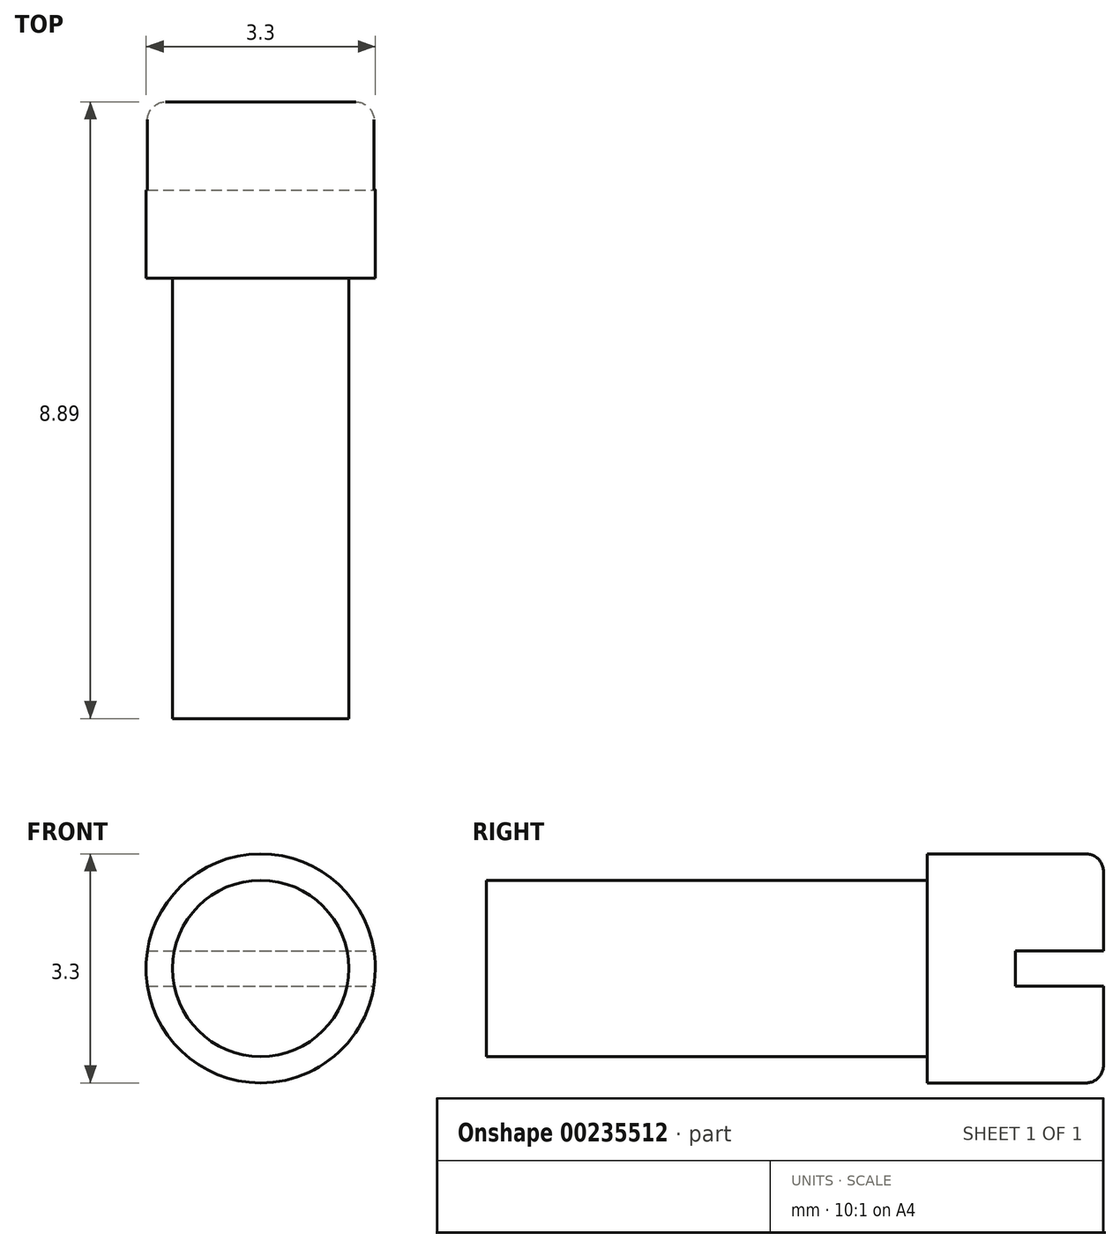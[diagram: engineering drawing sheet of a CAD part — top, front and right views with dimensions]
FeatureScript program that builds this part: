
annotation { "Feature Type Name" : "Feature", "Feature Type Description" : "" }
export const myFeature = defineFeature(function(context is Context, id is Id, definition is map)
    precondition{}
    {
        {
            var Q0;
            Q0=qCreatedBy(makeId("Front.planeOp"),FACE);
            var sketch = newSketch(context, id + "F0", { "sketchPlane" : qUnion([Q0])});
            skCircle(sketch, "E0", {"center": v(0, 0) * mm, "radius": 1.65 * mm});
            skCircle(sketch, "E1", {"center": v(0, 0) * mm, "radius": 1.27 * mm});
            skSolve(sketch);
        }
        {
            var Q0;
            Q0=makeQuery(id+"F0.imprint","IMPRINT",FACE,{"disambiguationData":[TD([[makeQuery(id+"F0.imprint","IMPRINT",EDGE,{"derivedFrom":sQuery(id+"F0.wireOp",EDGE,"E0")}),1.0]])]});
            extrude(context, id + "F1", {"entities" : qUnion([Q0]), "depth" : 2.54 * mm});
        }
        {
            var Q0;
            Q0=makeQuery(id+"F0.imprint","IMPRINT",FACE,{"disambiguationData":[TD([[makeQuery(id+"F0.imprint","IMPRINT",EDGE,{"derivedFrom":sQuery(id+"F0.wireOp",EDGE,"E1")}),1.0]])]});
            extrude(context, id + "F2", {"entities" : qUnion([Q0]), "operationType" : NewBodyOperationType.ADD, "depth" : 8.9 * mm});
        }
        {
            var Q0;
            Q0=makeQuery(id+"F1.opExtrude","CAP_EDGE",EDGE,{"disambiguationData":[OSD([sQuery(id+"F0.wireOp",EDGE,"E0")])],"isStart":true});
            fillet(context, id + "F3", {"entities" : qUnion([Q0]), "radius" : 0.25 * mm, "tangentPropagation" : true, "allowEdgeOverflow" : false});
        }
        {
            var Q0;
            Q0=makeQuery(id+"F0.imprint","IMPRINT",FACE,{"disambiguationData":[TD([[makeQuery(id+"F0.imprint","IMPRINT",EDGE,{"derivedFrom":sQuery(id+"F0.wireOp",EDGE,"E1")}),1.0]])]});
            var sketch = newSketch(context, id + "F4", { "sketchPlane" : qUnion([Q0])});
            skLineSegment(sketch, "E2", {"start": v(-1.63, 0.25) * mm, "end": v(1.63, 0.25) * mm});
            skLineSegment(sketch, "E3", {"start": v(-1.63, -0.25) * mm, "end": v(1.63, -0.25) * mm});
            skArc(sketch, "E4.0", {"start": v(-1.63, 0.25) * mm, "mid": v(-1.65, 0) * mm, "end": v(-1.63, -0.25) * mm});
            skArc(sketch, "E5.trimOffspring", {"start": v(1.63, -0.25) * mm, "mid": v(1.65, 0) * mm, "end": v(1.63, 0.25) * mm});
            skSolve(sketch);
        }
        {
            var Q0;
            Q0 = qSketchRegion(id + "F4", true);
            extrude(context, id + "F5", {"entities" : qUnion([Q0]), "operationType" : NewBodyOperationType.REMOVE, "depth" : 1.27 * mm});
        }
    });
